# Revit family: Рондо-2
name_source: partatom
category: Осветительные приборы
units: mm (PartAtom-declared; Revit-internal decimal feet)

## family parameters
Всегда вертикально = Да
Источник света = Да
На основе рабочей плоскости = Нет
Общий = Нет
При загрузке вырезать с полостями = Нет
Размер круглого соединителя = Использовать диаметр
Тип детали = Нормальный
Точка расчета площади = Нет

## types (11) — shared parameters
ADSK_URL страницы изделия = https://www.allfresco.ru
ADSK_Единица измерения = шт.
ADSK_Завод-изготовитель = ALFRESCO
ADSK_Количество фаз = 2
ADSK_Модель = Рондо-2 ДТУ-88-AF
ADSK_Напряжение = 220 В
ADSK_Полная мощность = 0 В·А
ADSK_Ток = 0 А
ADSK_Энергоэффективность = 110 лм/Вт
H_дверка = 500 мм
IP Class = IP 67
a1_фланец = 200 мм
a_фланец = 280 мм
d_верх столба = 70 мм
d_основание столба = 110 мм
d_отверстие фланец = 22 мм
h1_отступ до верхнего светильника = 70 мм
h2_расстояние между светильниками = 430 мм
h_дверь = 500 мм
h_пластина = 5 мм
h_рассеиватель = 5 мм
h_светильник = 146 мм
h_столб = 3000 мм
h_установки светильников = 1000 мм
h_фланец = 10 мм
r светильник = 445 мм
r1_дверь = 45 мм
r2_дверь = 55 мм
r_верх столба = 35 мм
r_отверстие фланец = 11 мм
r_пластина = 50 мм
r_рассеиватель = 440 мм
r_столб = 30 мм
Блок аварийного питания = Нет
Класс защиты = 1
Класс пожароопасности = F (светильники предназначены для установки непосредственно на поверхность из нормально воспламеняемых материалов)
Климатическая зона = УХЛ1
Корпус светильника = Серый металл
Материал рассеивателя = Светотехнический ПК
Область использования = Парки, скверы, общественные пространства, городская инфраструктура
Полная установленная мощность = 0 В·А
Рассеиватель = Белый_светодиод
Светофильтр = 16777215
Смещение цветовой температуры при затухании лампы = <Нет>
Таблица выбора = Таблица параметров светильников — копия
Температура эксплуатации = -40 +50
Тип ИС = LED-модуль
Тип КСС = ШБ (широкая боковая)
Тип ПРА = -
Тип продукции = LED-светильник
Угол наклона = 90.00°
Цветоывая температура = 2700-5500
zero-valued in all types: ADSK_Количество фаз числовое, ADSK_Коэффициент мощности

## per-type parameters (varying)
| type | 2 светильника | 3 светильника | ADSK_Артикул | ADSK_Масса | ADSK_Масса_Текст | ADSK_Наименование | ADSK_Номинальная мощность | ADSK_Размер_Высота | ADSK_Фактическая мощность | h_сужения столба | Артикул | Файл фотометрической сетки |
| ДТУ8820 Светодиодный светильник Рондо-2 ДТУ-88-AF-ДТУП891(25Вт)-4,0 | Нет | Нет | ДТУ8820 | 37 | 37 | ДТУ8820 Светодиодный светильник Рондо-2 ДТУ-88-AF-ДТУП891(25Вт)-4.0 | 25 Вт | 4000 мм | 25 Вт | 2990 мм | 8820 мм | DTUP-891-AF RONDO-2 25W 146x60.ies |
| ДТУ8837 Светодиодный светильник Рондо-2 ДТУ-88-AF-ДТУП892(50Вт)-4,0 | Нет | Нет | ДТУ8837 | 37 | 37 | ДТУ8837 Светодиодный светильник Рондо-2 ДТУ-88-AF-ДТУП892(50Вт)-4.0 | 50 Вт | 4000 мм | 50 Вт | 2990 мм | 8837 мм | DTUP-892-AF RONDO-2 50W 146x60.ies |
| ДТУ8822 Светодиодный светильник Рондо-2 ДТУ-88-AF-ДТУП892(50Вт)-5,0 | Нет | Нет | ДТУ8822 | 44 | 44 | ДТУ8822 Светодиодный светильник Рондо-2 ДТУ-88-AF-ДТУП892(50Вт)-5.0 | 50 Вт | 5000 мм | 50 Вт | 3990 мм | 8822 мм | DTUP-892-AF RONDO-2 50W 146x60.ies |
| ДТУ8834 Светодиодный светильник Рондо-2 ДТУ-88-AF-ДТУП891(25Вт)-6,0 | Нет | Нет | ДТУ8834 | 53 | 53 | ДТУ8834 Светодиодный светильник Рондо-2 ДТУ-88-AF-ДТУП891(25Вт)-6.0 | 25 Вт | 6000 мм | 25 Вт | 4990 мм | 8834 мм | DTUP-891-AF RONDO-2 25W 146x60.ies |
| ДТУ8833 Светодиодный светильник Рондо-2 ДТУ-88-AF-ДТУП892(50Вт)-6,0 | Нет | Нет | ДТУ8833 | 53 | 53 | ДТУ8833 Светодиодный светильник Рондо-2 ДТУ-88-AF-ДТУП892(50Вт)-6.0 | 50 Вт | 6000 мм | 50 Вт | 4990 мм | 8833 мм | DTUP-892-AF RONDO-2 50W 146x60.ies |
| ДТУ8825 Светодиодный светильник Рондо-2 ДТУ-88-AF-ДТУП893(75Вт)-6,0 | Нет | Нет | ДТУ8825 | 53 | 53 | ДТУ8825 Светодиодный светильник Рондо-2 ДТУ-88-AF-ДТУП893(75Вт)-6.0 | 75 Вт | 6000 мм | 75 Вт | 4990 мм | 8825 мм | DTUP-893-AF RONDO-2 75W 146x60.ies |
| ДТУ8843 Светодиодный светильник Рондо-2 ДТУ-88-AF-ДТУП892(50Вт)_ДТУП892(50Вт)(3,5)-4,0 | Да | Нет | ДТУ8843 | 47 | 47 | ДТУ8843 Светодиодный светильник Рондо-2 ДТУ-88-AF-ДТУП892(50Вт)_ДТУП892(50Вт)(3.5)-4.0 | 50 Вт | 4000 мм | 50 Вт | 2990 мм | 8843 мм | DTUP-893-AF RONDO-2 75W 146x60.ies |
| ДТУ8830 Светодиодный светильник Рондо-2 ДТУ-88-AF-ДТУП891(25Вт)_ДТУП891(25Вт)(4,5)-5,0 | Да | Нет | ДТУ8830 | 55 | 55 | ДТУ8830 Светодиодный светильник Рондо-2 ДТУ-88-AF-ДТУП891(25Вт)_ДТУП891(25Вт)(4.5)-5.0 | 50 Вт | 5000 мм | 50 Вт | 3990 мм | 8830 мм | DTUP-892-AF RONDO-2 50W 146x60.ies |
| ДТУ8832 Светодиодный светильник Рондо-2 ДТУ-88-AF-ДТУП891(25Вт)_ДТУП891(25Вт)(5,5)-6,0 | Да | Нет | ДТУ8832 | 63 | 63 | ДТУ8832 Светодиодный светильник Рондо-2 ДТУ-88-AF-ДТУП891(25Вт)_ДТУП891(25Вт)(5.5)-6.0 | 50 Вт | 6000 мм | 50 Вт | 4990 мм | 8832 мм | DTUP-892-AF RONDO-2 50W 146x60.ies |
| ДТУ8827 Светодиодный светильник Рондо-2 ДТУ-88-AF-ДТУП893(75Вт)_ДТУП892(50Вт)(5,5)-6,0 | Да | Нет | ДТУ8827 | 63 | 63 | ДТУ8827 Светодиодный светильник Рондо-2 ДТУ-88-AF-ДТУП893(75Вт)_ДТУП892(50Вт)(5.5)-6.0 | 125 Вт | 6000 мм | 125 Вт | 4990 мм | 8827 мм | DTUP-893-AF RONDO-2 75W 146x60.ies |
| ДТУ8831 Светодиодный св-к Рондо-2 ДТУ-88-AF-ДТУП891(25Вт)_ДТУП891(25Вт)(4,5)_ДТУП891(25Вт)(4,0)-5,0 | Да | Да | ДТУ8831 | 74 | 74 | ДТУ8831 Светодиодный св-к Рондо-2 ДТУ-88-AF-ДТУП891(25Вт)_ДТУП891(25Вт)(4.5)_ДТУП891(25Вт)(4.0)-5.0 | 75 Вт | 5000 мм | 75 Вт | 3990 мм | 8831 мм | DTUP-893-AF RONDO-2 75W 146x60.ies |

## geometry (parser evidence)
native form markers: Blend x4
no freeform markers — native parametric forms only
